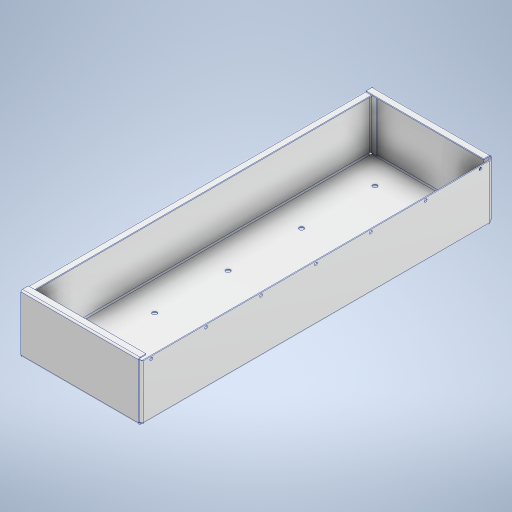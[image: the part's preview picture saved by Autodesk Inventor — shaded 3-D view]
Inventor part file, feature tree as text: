
AUTODESK INVENTOR PART (.ipt)
format: ipt  version: 2023 (Build 270158000, 158)  size: 495,104 bytes
history: native  units: in
note: dims shown in document units (in); Inventor stores cm internally (conversion verified against a paired STEP export)
features: sheet_metal_op x16, sketch x12, other x10, hole x2, pattern_linear x2
ambient origin geometry x8: Origin, YZ Plane, XZ Plane, XY Plane, X Axis, Y Axis, Z Axis, Center Point
bodies: Solid1 (feature_tree)
feature tree (42):
  sheet_metal_op  "Face1"
  hole  "Hole1"  [1 undecoded]
  pattern_linear  "Rectangular Pattern1"  Count1=30  [1 undecoded]
  sheet_metal_op  "Flange4"
  sheet_metal_op  "Flange5"
  sheet_metal_op  "Flange11"
  sketch  "Sketch21"  dims[d51=0.0312in]
  hole  "Hole2"  [1 undecoded]
  pattern_linear  "Rectangular Pattern2"  Count1=5  [1 undecoded]
  sheet_metal_op  "Flange14"
  sheet_metal_op  "Flange17"
  sketch  "Sketch1"  dims[d0=23.622in d1=7.874in d2=11.811in]
  other  "Plate1"
  sketch  "Sketch2"  dims[d3=3.937in d4=0.0625in]
  sketch  "Sketch6"  dims[d5=0.2969in d6=0.2953in d7=0.1476in d8=0.0984in d9=90.0deg d10=0.0625in]
  other  "Plate5"
  sheet_metal_op  "Bend4"
  sheet_metal_op  "Corner4"
  sketch  "Sketch7"  dims[d11=0.0in d12=1.9685in]
  other  "Plate6"
  sheet_metal_op  "Bend5"
  sheet_metal_op  "Corner5"
  sketch  "Sketch8"  dims[d13=2.0669in]
  sketch  "Sketch9"  dims[d14=0.7874in d16=3.937in]
  sketch  "Sketch17"  dims[d17=1.9685in d19=4.9213in]
  other  "Plate12"
  sheet_metal_op  "Bend11"
  sheet_metal_op  "Corner11"
  sketch  "Sketch20"  dims[d50=0.0625in]
  sketch  "Sketch22"  dims[d52=0.125in]
  sketch  "Sketch23"  dims[d53=0.0625in]
  other  "Plate15"
  sheet_metal_op  "Bend14"
  sheet_metal_op  "Corner14"
  sketch  "Sketch26"  dims[d54=3.8465in d55=90.0deg d56=0.0787in d57=0.25in d58=0.0625in d59=0.0625in d60=0.0625in d61=0.0312in d62=0.125in d63=0.0625in d64=3.937in d65=90.0deg d66=0.0787in d67=0.25in d68=0.0625in d69=0.0625in d70=0.0in d71=0.0in d72=0.0in d73=0.0in d78=0.0625in d79=0.0in d80=0.0625in d81=0.0in d147=0.0625in d148=0.0312in d149=0.125in d150=0.0625in d151=0.5in d152=90.0deg d153=0.0787in d154=0.25in d155=0.0625in d156=0.0625in d177=0.194in d178=0.2953in d179=0.1476in d180=0.0984in d181=90.0deg d182=0.0625in d183=0.8108in d185=0.5in d186=2.7559in d188=3.6755in d190=0.0625in d191=0.0in d192=0.162in d193=0.2073in d195=0.0625in d196=0.0in d197=0.1in d198=0.0625in d199=0.0312in d200=0.125in d201=0.0625in d202=0.5in d203=90.0deg d204=0.0591in d205=0.25in d206=0.0625in d207=0.0625in d228=0.0625in d229=0.0312in d230=0.125in d231=0.0625in d232=0.5in d233=90.0deg d234=0.0394in d235=0.25in d236=0.0625in d237=0.0625in d238=0.1969in d239=0.1969in d240=0.1662in d241=0.1662in]
  other  "Plate18"
  sheet_metal_op  "Bend17"
  sheet_metal_op  "Corner17"
  other  "Cut2"
  other  "Cut3"
  other  "Cut4"
  other  "Cut5"
note: 4 required parameter values undecoded (feature->parameter linkage not recoverable at this tier; creation-order binding heuristic only, values carry confidence <= 0.55)
